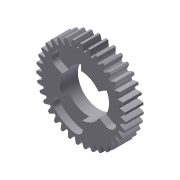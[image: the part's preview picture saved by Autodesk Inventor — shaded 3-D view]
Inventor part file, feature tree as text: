
AUTODESK INVENTOR PART (.ipt)
format: ipt  version: 2013 (Build 170138000, 138)  size: 355,328 bytes
history: native  units: mm (DEFAULTED — no unit token found)
features: sketch x4, extrude x3, plane x3, other x3, pattern_circular x1
ambient origin geometry x8: Origin, YZ Plane, XZ Plane, XY Plane, X Axis, Y Axis, Z Axis, Center Point
bodies: Solid1 (feature_tree)
feature tree (14):
  extrude  "Extrusion1"  Depth=9.525mm TaperAngle=0.0deg
  plane  "Work Plane1"
  plane  "Work Plane2"
  plane  "Work Plane3"
  other  "Spur Gear"
  extrude  "Extrusion4"  Depth=76.2mm TaperAngle=0.0deg
  extrude  "Extrusion5"  Depth=22.225mm
  pattern_circular  "Circular Pattern1"  [2 undecoded]
  sketch  "Sketch1"  dims[d0=46.99mm d1=9.525mm d2=0.0mm]
  sketch  "Sketch2"  dims[d3=44.45mm d4=76.2mm d5=0.0mm]
  other  "Srf1"
  sketch  "Sketch6"  dims[d6=0.0mm d7=0.897598mm d31=22.225mm]
  sketch  "Sketch7"  dims[d32=25.4mm d33=0.0mm d34=19.05mm d35=11.170107mm d36=3.81mm d37=3.6576mm d38=0.0mm d39=30.0mm d40=360.0deg]
  other  "Pitch Diameter"
note: 2 required parameter values undecoded (feature->parameter linkage not recoverable at this tier; creation-order binding heuristic only, values carry confidence <= 0.55)
